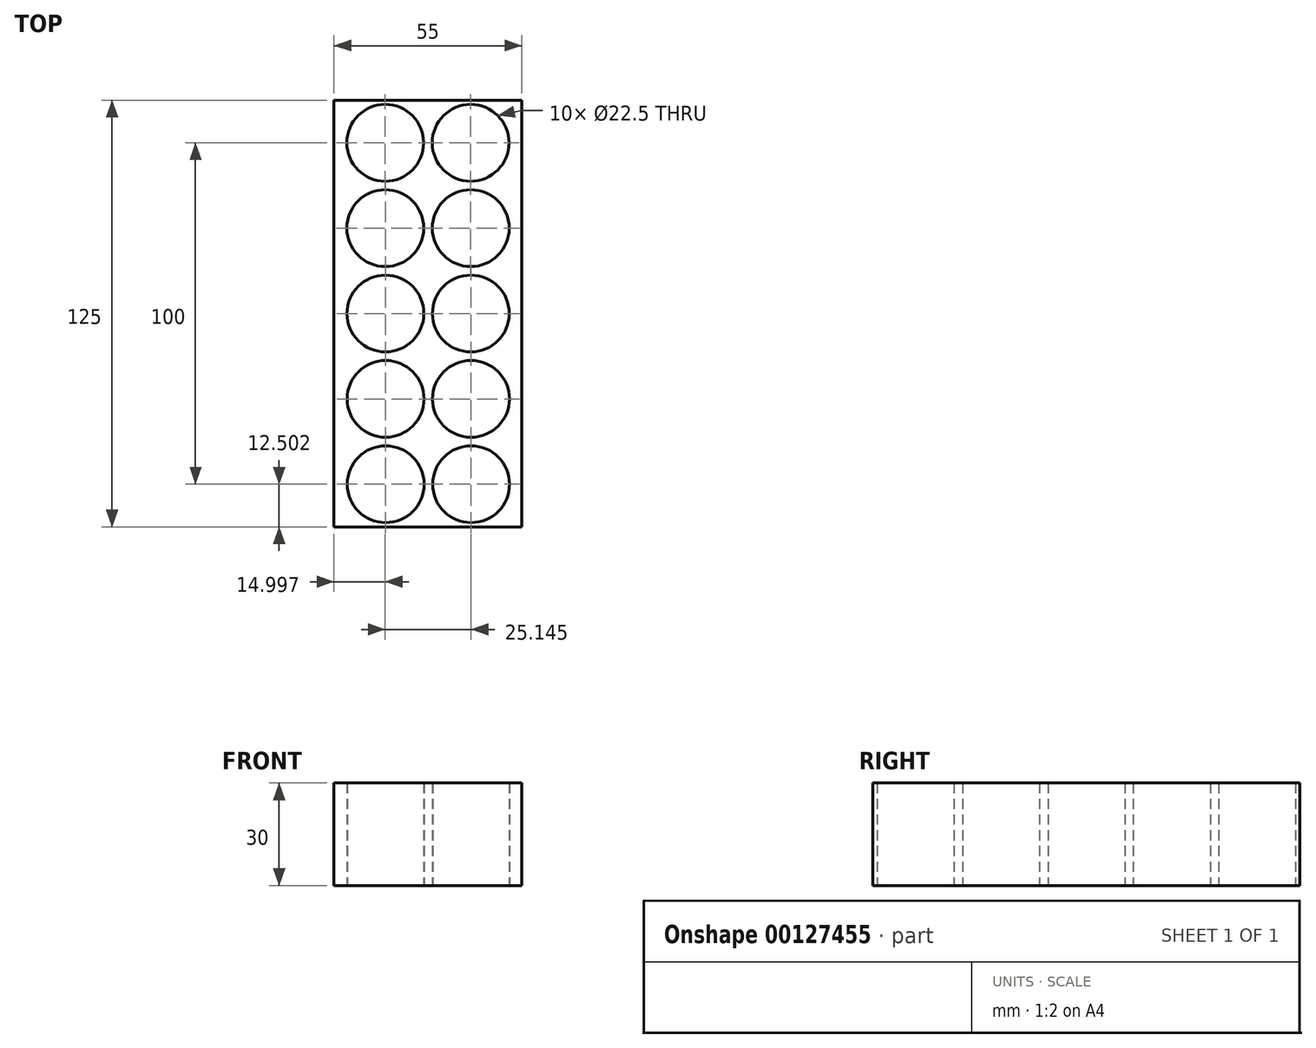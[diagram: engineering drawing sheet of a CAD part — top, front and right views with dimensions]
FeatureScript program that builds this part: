
annotation { "Feature Type Name" : "Feature", "Feature Type Description" : "" }
export const myFeature = defineFeature(function(context is Context, id is Id, definition is map)
    precondition{}
    {
        {
            var Q0;
            Q0=qCreatedBy(makeId("Top.planeOp"),FACE);
            var sketch = newSketch(context, id + "F0", { "sketchPlane" : qUnion([Q0])});
            skCircle(sketch, "E0", {"center": v(-10.21, 7.36) * mm, "radius": 11.25 * mm});
            skLineSegment(sketch, "E1.bottom", {"start": v(-25.21, 19.86) * mm, "end": v(29.79, 19.86) * mm});
            skLineSegment(sketch, "E1.top", {"start": v(-25.21, -105.14) * mm, "end": v(29.79, -105.14) * mm});
            skLineSegment(sketch, "E1.left", {"start": v(-25.21, 19.86) * mm, "end": v(-25.21, -105.14) * mm});
            skLineSegment(sketch, "E1.right", {"start": v(29.79, 19.86) * mm, "end": v(29.79, -105.14) * mm});
            skCircle(sketch, "E2.0.1.0", {"center": v(-10.18, -17.64) * mm, "radius": 11.25 * mm});
            skCircle(sketch, "E2.0.2.0", {"center": v(-10.14, -42.64) * mm, "radius": 11.25 * mm});
            skCircle(sketch, "E2.0.3.0", {"center": v(-10.1, -67.64) * mm, "radius": 11.25 * mm});
            skCircle(sketch, "E2.0.4.0", {"center": v(-10.07, -92.64) * mm, "radius": 11.25 * mm});
            skCircle(sketch, "E2.1.0.0", {"center": v(14.79, 7.36) * mm, "radius": 11.25 * mm});
            skCircle(sketch, "E2.1.1.0", {"center": v(14.82, -17.64) * mm, "radius": 11.25 * mm});
            skCircle(sketch, "E2.1.2.0", {"center": v(14.86, -42.64) * mm, "radius": 11.25 * mm});
            skCircle(sketch, "E2.1.3.0", {"center": v(14.9, -67.64) * mm, "radius": 11.25 * mm});
            skCircle(sketch, "E2.1.4.0", {"center": v(14.93, -92.64) * mm, "radius": 11.25 * mm});
            skLineSegment(sketch, "E2.direction1", {"start": v(-10.21, 7.36) * mm, "end": v(14.79, 7.36) * mm, "construction": true});
            skLineSegment(sketch, "E2.direction2", {"start": v(-10.21, 7.36) * mm, "end": v(-10.18, -17.64) * mm, "construction": true});
            skSolve(sketch);
        }
        {
            var Q0;
            Q0=makeQuery(id+"F0.imprint","IMPRINT",FACE,{"disambiguationData":[TD([[makeQuery(id+"F0.imprint","IMPRINT",EDGE,{"derivedFrom":sQuery(id+"F0.wireOp",EDGE,"E0")}),-1.0]])]});
            extrude(context, id + "F1", {"entities" : qUnion([Q0]), "depth" : 30 * mm});
        }
    });
